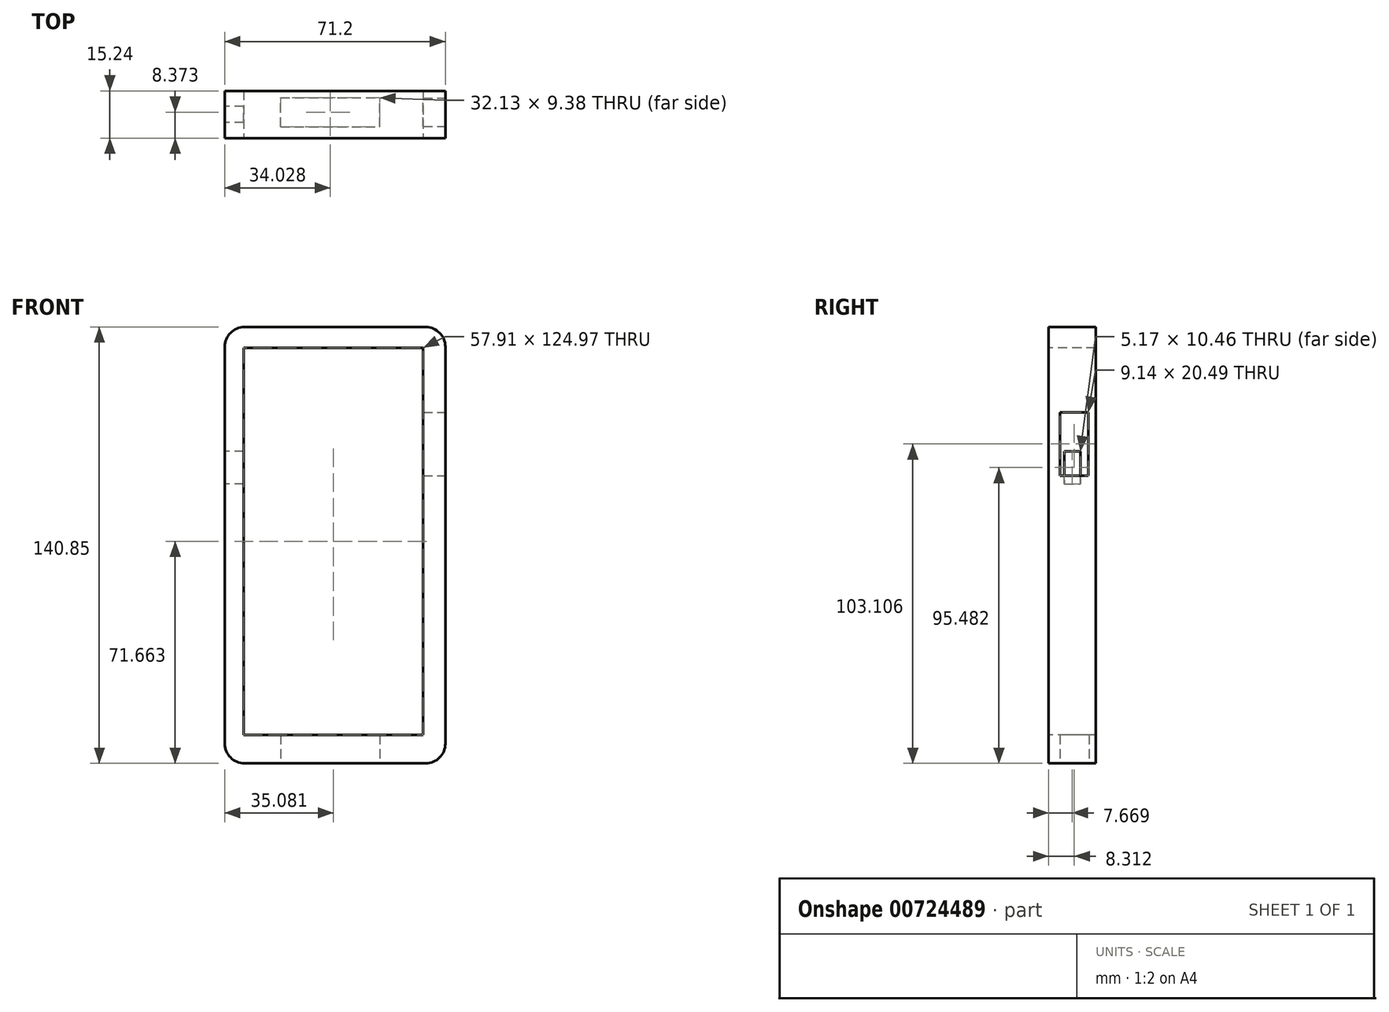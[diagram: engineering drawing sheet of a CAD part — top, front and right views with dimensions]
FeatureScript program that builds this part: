
annotation { "Feature Type Name" : "Feature", "Feature Type Description" : "" }
export const myFeature = defineFeature(function(context is Context, id is Id, definition is map)
    precondition{}
    {
        {
            var Q0;
            Q0=qCreatedBy(makeId("Front.planeOp"),FACE);
            var sketch = newSketch(context, id + "F0", { "sketchPlane" : qUnion([Q0])});
            skLineSegment(sketch, "E0", {"start": v(-53.37, 87.4) * mm, "end": v(-53.37, -40.74) * mm});
            skLineSegment(sketch, "E1", {"start": v(-47.02, 93.76) * mm, "end": v(11.48, 93.76) * mm});
            skLineSegment(sketch, "E2", {"start": v(17.83, 87.4) * mm, "end": v(17.83, -40.74) * mm});
            skLineSegment(sketch, "E3", {"start": v(11.48, -47.09) * mm, "end": v(-47.02, -47.09) * mm});
            skPoint(sketch, "E4.visualSharp", {"position": v(-53.37, 93.76) * mm});
            skArc(sketch, "E4.filletArc", {"start": v(-47.02, 93.76) * mm, "mid": v(-51.51, 91.9) * mm, "end": v(-53.37, 87.4) * mm});
            skPoint(sketch, "E5.visualSharp", {"position": v(17.83, 93.76) * mm});
            skArc(sketch, "E5.filletArc", {"start": v(17.83, 87.4) * mm, "mid": v(15.97, 91.9) * mm, "end": v(11.48, 93.76) * mm});
            skPoint(sketch, "E6.visualSharp", {"position": v(17.83, -47.09) * mm});
            skArc(sketch, "E6.filletArc", {"start": v(11.48, -47.09) * mm, "mid": v(15.97, -45.23) * mm, "end": v(17.83, -40.74) * mm});
            skPoint(sketch, "E7.visualSharp", {"position": v(-53.37, -47.09) * mm});
            skArc(sketch, "E7.filletArc", {"start": v(-53.37, -40.74) * mm, "mid": v(-51.51, -45.23) * mm, "end": v(-47.02, -47.09) * mm});
            skLineSegment(sketch, "E8", {"start": v(-53.37, 75.77) * mm, "end": v(-30.05, 75.77) * mm});
            skSolve(sketch);
        }
        {
            var Q0;
            Q0=makeQuery(id+"F0.imprint","IMPRINT",FACE,{"disambiguationData":[TD([[makeQuery(id+"F0.imprint","IMPRINT",EDGE,{"derivedFrom":sQuery(id+"F0.wireOp",EDGE,"E1")}),-1.0]])]});
            extrude(context, id + "F1", {"entities" : qUnion([Q0]), "depth" : 15.24 * mm, "offsetDistance" : 25.4 * mm});
        }
        {
            var Q0;
            Q0=makeQuery(id+"F1.opExtrude","CAP_FACE",FACE,{"disambiguationData":[OSD([sQuery(id+"F0.wireOp",EDGE,"E0"),sQuery(id+"F0.wireOp",EDGE,"E1"),sQuery(id+"F0.wireOp",EDGE,"E2"),sQuery(id+"F0.wireOp",EDGE,"E3"),sQuery(id+"F0.wireOp",EDGE,"E4.filletArc"),sQuery(id+"F0.wireOp",EDGE,"E5.filletArc"),sQuery(id+"F0.wireOp",EDGE,"E6.filletArc"),sQuery(id+"F0.wireOp",EDGE,"E7.filletArc")])],"isStart":false});
            var sketch = newSketch(context, id + "F2", { "sketchPlane" : qUnion([Q0])});
            skLineSegment(sketch, "E9", {"start": v(-40.6, 86.31) * mm, "end": v(-40.6, -35.57) * mm});
            skLineSegment(sketch, "E10", {"start": v(-40.6, -35.57) * mm, "end": v(5.34, -35.57) * mm});
            skLineSegment(sketch, "E11", {"start": v(5.34, -35.57) * mm, "end": v(5.34, 80.75) * mm});
            skLineSegment(sketch, "E12", {"start": v(5.34, 80.75) * mm, "end": v(-40.6, 86.31) * mm});
            skLineSegment(sketch, "E13", {"start": v(5.34, 86.31) * mm, "end": v(5.34, 80.75) * mm});
            skSolve(sketch);
        }
        {
            var Q0;
            Q0=makeQuery(id+"F2.imprint","IMPRINT",FACE,{"disambiguationData":[TD([[makeQuery(id+"F2.imprint","IMPRINT",EDGE,{"derivedFrom":sQuery(id+"F2.wireOp",EDGE,"E9")}),-1.0]])]});
            var sketch = newSketch(context, id + "F3", { "sketchPlane" : qUnion([Q0])});
            skLineSegment(sketch, "E14", {"start": v(-47.25, 87.06) * mm, "end": v(10.67, 87.06) * mm});
            skLineSegment(sketch, "E15", {"start": v(10.67, 87.06) * mm, "end": v(10.67, -37.91) * mm});
            skLineSegment(sketch, "E16", {"start": v(10.67, -37.91) * mm, "end": v(-47.25, 87.06) * mm});
            skLineSegment(sketch, "E17", {"start": v(-47.25, 87.06) * mm, "end": v(-47.25, -35.7) * mm});
            skLineSegment(sketch, "E18", {"start": v(-47.25, -35.7) * mm, "end": v(10.67, -37.91) * mm});
            skLineSegment(sketch, "E19", {"start": v(10.67, -37.91) * mm, "end": v(-47.25, -37.91) * mm});
            skLineSegment(sketch, "E20", {"start": v(-47.25, -37.91) * mm, "end": v(-47.25, -35.7) * mm});
            skSolve(sketch);
        }
        {
            var Q0;
            Q0 = qSketchRegion(id + "F3", true);
            extrude(context, id + "F4", {"entities" : qUnion([Q0]), "operationType" : NewBodyOperationType.REMOVE, "oppositeDirection" : true, "depth" : 25.4 * mm, "offsetDistance" : 25.4 * mm});
        }
        {
            var Q0;
            Q0=makeQuery(id+"F1.opExtrude","SWEPT_FACE",FACE,{"disambiguationData":[OSD([sQuery(id+"F0.wireOp",EDGE,"E0")])]});
            var sketch = newSketch(context, id + "F5", { "sketchPlane" : qUnion([Q0])});
            skLineSegment(sketch, "E21.0", {"start": v(15.24, 93.76) * mm, "end": v(0, 93.76) * mm});
            skLineSegment(sketch, "E22", {"start": v(7.62, 93.76) * mm, "end": v(7.62, 53.62) * mm});
            skLineSegment(sketch, "E23", {"start": v(7.62, 53.62) * mm, "end": v(7.62, 43.16) * mm});
            skLineSegment(sketch, "E24", {"start": v(7.62, 43.16) * mm, "end": v(4.99, 43.16) * mm});
            skLineSegment(sketch, "E25", {"start": v(4.99, 43.16) * mm, "end": v(4.99, 53.62) * mm});
            skLineSegment(sketch, "E26", {"start": v(4.99, 53.62) * mm, "end": v(10.15, 53.62) * mm});
            skLineSegment(sketch, "E27", {"start": v(10.15, 53.62) * mm, "end": v(10.15, 43.16) * mm});
            skLineSegment(sketch, "E28", {"start": v(10.15, 43.16) * mm, "end": v(7.62, 43.16) * mm});
            skSolve(sketch);
        }
        {
            var Q0;
            Q0 = qSketchRegion(id + "F5", true);
            extrude(context, id + "F6", {"entities" : qUnion([Q0]), "operationType" : NewBodyOperationType.REMOVE, "oppositeDirection" : true, "depth" : 25.4 * mm, "offsetDistance" : 25.4 * mm});
        }
        {
            var Q0;
            Q0=makeQuery(id+"F1.opExtrude","SWEPT_FACE",FACE,{"disambiguationData":[OSD([sQuery(id+"F0.wireOp",EDGE,"E2")])]});
            var sketch = newSketch(context, id + "F7", { "sketchPlane" : qUnion([Q0])});
            skLineSegment(sketch, "E29.0", {"start": v(-15.24, 93.76) * mm, "end": v(0, 93.76) * mm});
            skLineSegment(sketch, "E30", {"start": v(-7.62, 66.26) * mm, "end": v(-7.62, 45.94) * mm});
            skLineSegment(sketch, "E31", {"start": v(-7.62, 66.26) * mm, "end": v(-11.5, 66.26) * mm});
            skLineSegment(sketch, "E32", {"start": v(-11.5, 66.26) * mm, "end": v(-11.5, 45.77) * mm});
            skLineSegment(sketch, "E33", {"start": v(-11.5, 45.77) * mm, "end": v(-2.36, 45.77) * mm});
            skLineSegment(sketch, "E34", {"start": v(-2.36, 45.77) * mm, "end": v(-2.36, 66.26) * mm});
            skLineSegment(sketch, "E35", {"start": v(-2.36, 66.26) * mm, "end": v(-7.62, 66.26) * mm});
            skSolve(sketch);
        }
        {
            var Q0;
            Q0 = qSketchRegion(id + "F7", true);
            extrude(context, id + "F8", {"entities" : qUnion([Q0]), "operationType" : NewBodyOperationType.REMOVE, "oppositeDirection" : true, "depth" : 25.4 * mm, "offsetDistance" : 25.4 * mm});
        }
        {
            var Q0;
            Q0=makeQuery(id+"F1.opExtrude","SWEPT_FACE",FACE,{"disambiguationData":[OSD([sQuery(id+"F0.wireOp",EDGE,"E3")])]});
            var sketch = newSketch(context, id + "F9", { "sketchPlane" : qUnion([Q0])});
            skLineSegment(sketch, "E36", {"start": v(-35.4, 11.55) * mm, "end": v(-35.4, 2.18) * mm});
            skLineSegment(sketch, "E37", {"start": v(-35.4, 2.18) * mm, "end": v(-3.28, 2.18) * mm});
            skLineSegment(sketch, "E38", {"start": v(-35.4, 11.55) * mm, "end": v(-3.28, 11.55) * mm});
            skLineSegment(sketch, "E39", {"start": v(-3.28, 11.55) * mm, "end": v(-3.28, 2.18) * mm});
            skSolve(sketch);
        }
        {
            var Q0;
            Q0 = qSketchRegion(id + "F9", true);
            extrude(context, id + "F10", {"entities" : qUnion([Q0]), "operationType" : NewBodyOperationType.REMOVE, "oppositeDirection" : true, "depth" : 25.4 * mm, "offsetDistance" : 25.4 * mm});
        }
    });
